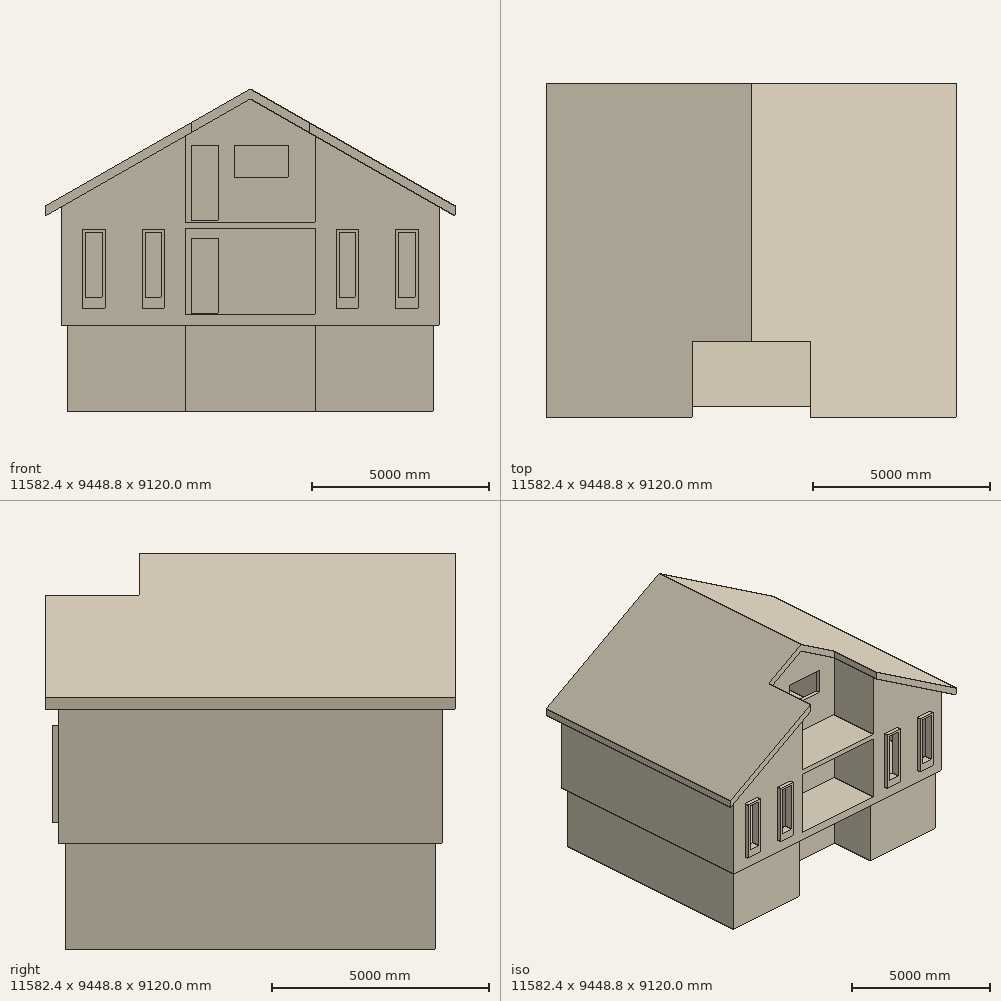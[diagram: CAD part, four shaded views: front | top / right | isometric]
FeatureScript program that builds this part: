
annotation { "Feature Type Name" : "Feature", "Feature Type Description" : "" }
export const myFeature = defineFeature(function(context is Context, id is Id, definition is map)
    precondition{}
    {
        {
            var Q0;
            Q0=qCreatedBy(makeId("Top.planeOp"),FACE);
            var sketch = newSketch(context, id + "F0", { "sketchPlane" : qUnion([Q0])});
            skLineSegment(sketch, "E0", {"start": v(0, 0) * mm, "end": v(3352.8, 0) * mm});
            skLineSegment(sketch, "E1", {"start": v(3352.8, 0) * mm, "end": v(3352.8, 1828.8) * mm});
            skLineSegment(sketch, "E2", {"start": v(3352.8, 1828.8) * mm, "end": v(7010.4, 1828.8) * mm});
            skLineSegment(sketch, "E3", {"start": v(7010.4, 1828.8) * mm, "end": v(7010.4, 0) * mm});
            skLineSegment(sketch, "E4", {"start": v(7010.4, 0) * mm, "end": v(10363.2, 0) * mm});
            skLineSegment(sketch, "E5", {"start": v(10363.2, 0) * mm, "end": v(10363.2, 8534.4) * mm});
            skLineSegment(sketch, "E6", {"start": v(10363.2, 8534.4) * mm, "end": v(7010.4, 8534.4) * mm});
            skLineSegment(sketch, "E7", {"start": v(7010.4, 8534.4) * mm, "end": v(7010.4, 7924.8) * mm});
            skLineSegment(sketch, "E8", {"start": v(7010.4, 7924.8) * mm, "end": v(3352.8, 7924.8) * mm});
            skLineSegment(sketch, "E9", {"start": v(3352.8, 7924.8) * mm, "end": v(3352.8, 8534.4) * mm});
            skLineSegment(sketch, "E10", {"start": v(3352.8, 8534.4) * mm, "end": v(0, 8534.4) * mm});
            skLineSegment(sketch, "E11", {"start": v(0, 8534.4) * mm, "end": v(0, 0) * mm});
            skSolve(sketch);
        }
        {
            var Q0;
            Q0 = qSketchRegion(id + "F0", true);
            extrude(context, id + "F1", {"entities" : qUnion([Q0]), "depth" : 2438.4 * mm});
        }
        {
            var Q0;
            Q0=makeQuery(id+"F1.opExtrude","CAP_FACE",FACE,{"disambiguationData":[OSD([sQuery(id+"F0.wireOp",EDGE,"E0"),sQuery(id+"F0.wireOp",EDGE,"E1"),sQuery(id+"F0.wireOp",EDGE,"E2"),sQuery(id+"F0.wireOp",EDGE,"E3"),sQuery(id+"F0.wireOp",EDGE,"E4"),sQuery(id+"F0.wireOp",EDGE,"E5"),sQuery(id+"F0.wireOp",EDGE,"E6"),sQuery(id+"F0.wireOp",EDGE,"E7"),sQuery(id+"F0.wireOp",EDGE,"E8"),sQuery(id+"F0.wireOp",EDGE,"E9"),sQuery(id+"F0.wireOp",EDGE,"E10"),sQuery(id+"F0.wireOp",EDGE,"E11")])],"isStart":false});
            var sketch = newSketch(context, id + "F2", { "sketchPlane" : qUnion([Q0])});
            skLineSegment(sketch, "E12.bottom", {"start": v(-152.4, -152.4) * mm, "end": v(10515.6, -152.4) * mm});
            skLineSegment(sketch, "E12.top", {"start": v(-152.4, 8686.8) * mm, "end": v(10515.6, 8686.8) * mm});
            skLineSegment(sketch, "E12.left", {"start": v(-152.4, -152.4) * mm, "end": v(-152.4, 8686.8) * mm});
            skLineSegment(sketch, "E12.right", {"start": v(10515.6, -152.4) * mm, "end": v(10515.6, 8686.8) * mm});
            skSolve(sketch);
        }
        {
            var Q0;
            Q0 = qSketchRegion(id + "F2", true);
            extrude(context, id + "F3", {"entities" : qUnion([Q0]), "operationType" : NewBodyOperationType.ADD, "depth" : 304.8 * mm});
        }
        {
            var Q0;
            Q0=makeQuery(id+"F3.opExtrude","CAP_FACE",FACE,{"disambiguationData":[OSD([sQuery(id+"F2.wireOp",EDGE,"E12.bottom"),sQuery(id+"F2.wireOp",EDGE,"E12.top"),sQuery(id+"F2.wireOp",EDGE,"E12.left"),sQuery(id+"F2.wireOp",EDGE,"E12.right")])],"isStart":false});
            var sketch = newSketch(context, id + "F4", { "sketchPlane" : qUnion([Q0])});
            skLineSegment(sketch, "E13", {"start": v(-152.4, -152.4) * mm, "end": v(3352.8, -152.4) * mm});
            skLineSegment(sketch, "E14", {"start": v(3352.8, -152.4) * mm, "end": v(3352.8, 1859.28) * mm});
            skLineSegment(sketch, "E15", {"start": v(3352.8, 1859.28) * mm, "end": v(7010.4, 1859.28) * mm});
            skLineSegment(sketch, "E16", {"start": v(7010.4, 1859.28) * mm, "end": v(7010.4, -152.4) * mm});
            skLineSegment(sketch, "E17", {"start": v(7010.4, -152.4) * mm, "end": v(10515.6, -152.4) * mm});
            skLineSegment(sketch, "E18", {"start": v(10515.6, -152.4) * mm, "end": v(10515.6, 8686.8) * mm});
            skLineSegment(sketch, "E19", {"start": v(10515.6, 8686.8) * mm, "end": v(-152.4, 8686.8) * mm});
            skLineSegment(sketch, "E20", {"start": v(-152.4, 8686.8) * mm, "end": v(-152.4, -152.4) * mm});
            skLineSegment(sketch, "E21.0", {"start": v(10363.2, 8534.4) * mm, "end": v(0, 8534.4) * mm});
            skLineSegment(sketch, "E21.1", {"start": v(10363.2, 0) * mm, "end": v(10363.2, 8534.4) * mm});
            skLineSegment(sketch, "E21.2", {"start": v(0, 8534.4) * mm, "end": v(0, 0) * mm});
            skLineSegment(sketch, "E21.3", {"start": v(7162.8, 0) * mm, "end": v(10363.2, 0) * mm});
            skLineSegment(sketch, "E21.4", {"start": v(0, 0) * mm, "end": v(3200.4, 0) * mm});
            skLineSegment(sketch, "E21.5", {"start": v(3200.4, 0) * mm, "end": v(3200.4, 2011.68) * mm});
            skLineSegment(sketch, "E21.6", {"start": v(3200.4, 2011.68) * mm, "end": v(7162.8, 2011.68) * mm});
            skLineSegment(sketch, "E21.7", {"start": v(7162.8, 2011.68) * mm, "end": v(7162.8, 0) * mm});
            skLineSegment(sketch, "E22.0", {"start": v(-147.4, 8681.8) * mm, "end": v(-147.4, -147.4) * mm});
            skLineSegment(sketch, "E22.1", {"start": v(10510.6, 8681.8) * mm, "end": v(-147.4, 8681.8) * mm});
            skLineSegment(sketch, "E22.2", {"start": v(10510.6, -147.4) * mm, "end": v(10510.6, 8681.8) * mm});
            skLineSegment(sketch, "E22.3", {"start": v(-147.4, -147.4) * mm, "end": v(3352.8, -147.4) * mm});
            skLineSegment(sketch, "E23.trimOffspring", {"start": v(7010.4, -147.4) * mm, "end": v(10510.6, -147.4) * mm});
            skSolve(sketch);
        }
        {
            var Q0;
            Q0 = qSketchRegion(id + "F4", true);
            extrude(context, id + "F5", {"entities" : qUnion([Q0]), "operationType" : NewBodyOperationType.ADD, "depth" : 6096 * mm});
        }
        {
            var Q0;
            Q0=makeQuery(id+"F5.boolean.opBoolean","MERGE",FACE,{"derivedFrom":[makeQuery(id+"F3.opExtrude","SWEPT_FACE",FACE,{"disambiguationData":[OSD([sQuery(id+"F2.wireOp",EDGE,"E12.bottom")])]}),makeQuery(id+"F5.opExtrude","SWEPT_FACE",FACE,{"disambiguationData":[OSD([sQuery(id+"F4.wireOp",EDGE,"E13")])]}),makeQuery(id+"F5.opExtrude","SWEPT_FACE",FACE,{"disambiguationData":[OSD([sQuery(id+"F4.wireOp",EDGE,"E17")])]})]});
            var sketch = newSketch(context, id + "F6", { "sketchPlane" : qUnion([Q0])});
            skLineSegment(sketch, "E24", {"start": v(5181.6, 2438.4) * mm, "end": v(5181.6, 8839.2) * mm, "construction": true});
            skLineSegment(sketch, "E25", {"start": v(5181.6, 8839.2) * mm, "end": v(-152.4, 5791.2) * mm});
            skLineSegment(sketch, "E26", {"start": v(-152.4, 5791.2) * mm, "end": v(-152.4, 14935.2) * mm});
            skLineSegment(sketch, "E27", {"start": v(-152.4, 14935.2) * mm, "end": v(10515.6, 14935.2) * mm});
            skLineSegment(sketch, "E28", {"start": v(10515.6, 14935.2) * mm, "end": v(10515.6, 5791.2) * mm});
            skLineSegment(sketch, "E29", {"start": v(10515.6, 5791.2) * mm, "end": v(5181.6, 8839.2) * mm});
            skSolve(sketch);
        }
        {
            var Q0;
            Q0 = qSketchRegion(id + "F6", true);
            extrude(context, id + "F7", {"entities" : qUnion([Q0]), "operationType" : NewBodyOperationType.REMOVE, "endBound" : BoundingType.THROUGH_ALL, "oppositeDirection" : true, "depth" : 30.48 * mm});
        }
        {
            var Q0;
            Q0=makeQuery(id+"F5.boolean.opBoolean","MERGE",FACE,{"derivedFrom":[makeQuery(id+"F3.opExtrude","SWEPT_FACE",FACE,{"disambiguationData":[OSD([sQuery(id+"F2.wireOp",EDGE,"E12.bottom")])]}),makeQuery(id+"F5.opExtrude","SWEPT_FACE",FACE,{"disambiguationData":[OSD([sQuery(id+"F4.wireOp",EDGE,"E13")])]}),makeQuery(id+"F5.opExtrude","SWEPT_FACE",FACE,{"disambiguationData":[OSD([sQuery(id+"F4.wireOp",EDGE,"E17")])]})]});
            var sketch = newSketch(context, id + "F8", { "sketchPlane" : qUnion([Q0])});
            skLineSegment(sketch, "E30.0", {"start": v(3352.8, 7794.17) * mm, "end": v(5181.6, 8839.2) * mm});
            skLineSegment(sketch, "E31.0", {"start": v(5181.6, 8839.2) * mm, "end": v(7010.4, 7794.17) * mm});
            skLineSegment(sketch, "E32.0", {"start": v(3352.8, 7794.17) * mm, "end": v(-152.4, 5791.2) * mm});
            skLineSegment(sketch, "E32.1", {"start": v(10515.6, 5791.2) * mm, "end": v(7010.4, 7794.17) * mm});
            skLineSegment(sketch, "E33", {"start": v(5181.6, 2743.2) * mm, "end": v(5181.6, 9120.04) * mm, "construction": true});
            skLineSegment(sketch, "E34", {"start": v(5181.6, 9120.04) * mm, "end": v(-609.6, 5810.79) * mm});
            skLineSegment(sketch, "E35", {"start": v(-609.6, 5810.79) * mm, "end": v(-609.6, 5529.94) * mm});
            skLineSegment(sketch, "E36", {"start": v(-609.6, 5529.94) * mm, "end": v(-152.4, 5791.2) * mm});
            skLineSegment(sketch, "E37.MirrorCS", {"start": v(5181.6, 9120.04) * mm, "end": v(10972.8, 5810.79) * mm});
            skLineSegment(sketch, "E38.MirrorCS", {"start": v(10972.8, 5810.79) * mm, "end": v(10972.8, 5529.94) * mm});
            skLineSegment(sketch, "E39.MirrorCS", {"start": v(10972.8, 5529.94) * mm, "end": v(10515.6, 5791.2) * mm});
            skSolve(sketch);
        }
        {
            var Q0;
            Q0 = qSketchRegion(id + "F8", true);
            extrude(context, id + "F9", {"entities" : qUnion([Q0]), "operationType" : NewBodyOperationType.ADD, "oppositeDirection" : true, "depth" : 9144 * mm, "hasSecondDirection" : true, "secondDirectionOppositeDirection" : false, "secondDirectionDepth" : 304.8 * mm});
        }
        {
            var Q0;
            {var subQ0=sQuery(id+"F2.wireOp",EDGE,"E12.bottom");Q0=makeQuery(id+"F5.boolean.opBoolean","SPLIT",FACE,{"disambiguationData":[TD([makeQuery(id+"F3.opExtrude","SWEPT_FACE",FACE,{"disambiguationData":[OSD([subQ0])]})])],"derivedFrom":makeQuery(id+"F3.opExtrude","CAP_FACE",FACE,{"disambiguationData":[OSD([subQ0,sQuery(id+"F2.wireOp",EDGE,"E12.top"),sQuery(id+"F2.wireOp",EDGE,"E12.left"),sQuery(id+"F2.wireOp",EDGE,"E12.right")])],"isStart":false})});}
            var sketch = newSketch(context, id + "F10", { "sketchPlane" : qUnion([Q0])});
            skLineSegment(sketch, "E40.bottom", {"start": v(3352.8, -152.4) * mm, "end": v(7010.4, -152.4) * mm});
            skLineSegment(sketch, "E40.top", {"start": v(3352.8, 1859.28) * mm, "end": v(7010.4, 1859.28) * mm});
            skLineSegment(sketch, "E40.left", {"start": v(3352.8, -152.4) * mm, "end": v(3352.8, 1859.28) * mm});
            skLineSegment(sketch, "E40.right", {"start": v(7010.4, -152.4) * mm, "end": v(7010.4, 1859.28) * mm});
            skSolve(sketch);
        }
        {
            var Q0;
            Q0 = qSketchRegion(id + "F10", true);
            extrude(context, id + "F11", {"entities" : qUnion([Q0]), "operationType" : NewBodyOperationType.ADD, "depth" : 2621.28 * mm, "hasSecondDirection" : true, "secondDirectionOppositeDirection" : false, "secondDirectionDepth" : 2438.4 * mm});
        }
        {
            var Q0;
            Q0=makeQuery(id+"F11.opExtrude","CAP_FACE",FACE,{"disambiguationData":[OSD([sQuery(id+"F10.wireOp",EDGE,"E40.bottom"),sQuery(id+"F10.wireOp",EDGE,"E40.top"),sQuery(id+"F10.wireOp",EDGE,"E40.left"),sQuery(id+"F10.wireOp",EDGE,"E40.right")])],"isStart":false});
            var sketch = newSketch(context, id + "F12", { "sketchPlane" : qUnion([Q0])});
            skLineSegment(sketch, "E41.top", {"start": v(3505.2, 1706.88) * mm, "end": v(6858, 1706.88) * mm});
            skLineSegment(sketch, "E41.left", {"start": v(3505.2, -762) * mm, "end": v(3505.2, 1706.88) * mm});
            skLineSegment(sketch, "E41.right", {"start": v(6858, -762) * mm, "end": v(6858, 1706.88) * mm});
            skLineSegment(sketch, "E42", {"start": v(3505.2, -762) * mm, "end": v(6858, -762) * mm});
            skSolve(sketch);
        }
        {
            var Q0;
            Q0 = qSketchRegion(id + "F12", true);
            extrude(context, id + "F13", {"entities" : qUnion([Q0]), "operationType" : NewBodyOperationType.REMOVE, "endBound" : BoundingType.THROUGH_ALL, "depth" : 30.48 * mm});
        }
        {
            var Q0;
            Q0=makeQuery(id+"F11.boolean.opBoolean","MERGE",FACE,{"derivedFrom":[makeQuery(id+"F5.boolean.opBoolean","MERGE",FACE,{"derivedFrom":[makeQuery(id+"F3.opExtrude","SWEPT_FACE",FACE,{"disambiguationData":[OSD([sQuery(id+"F2.wireOp",EDGE,"E12.bottom")])]}),makeQuery(id+"F5.opExtrude","SWEPT_FACE",FACE,{"disambiguationData":[OSD([sQuery(id+"F4.wireOp",EDGE,"E13")])]}),makeQuery(id+"F5.opExtrude","SWEPT_FACE",FACE,{"disambiguationData":[OSD([sQuery(id+"F4.wireOp",EDGE,"E17")])]})]}),makeQuery(id+"F11.opExtrude","SWEPT_FACE",FACE,{"disambiguationData":[OSD([sQuery(id+"F10.wireOp",EDGE,"E40.bottom")])]})]});
            var sketch = newSketch(context, id + "F14", { "sketchPlane" : qUnion([Q0])});
            skLineSegment(sketch, "E43.0", {"start": v(5181.6, 9120.04) * mm, "end": v(6858, 8162.1) * mm, "construction": true});
            skLineSegment(sketch, "E43.1", {"start": v(5181.6, 9120.04) * mm, "end": v(3505.2, 8162.1) * mm, "construction": true});
            skLineSegment(sketch, "E44", {"start": v(5181.6, 9120.04) * mm, "end": v(5181.6, 2224.24) * mm, "construction": true});
            skLineSegment(sketch, "E45.bottom", {"start": v(533.4, 3230.88) * mm, "end": v(990.6, 3230.88) * mm});
            skLineSegment(sketch, "E45.top", {"start": v(533.4, 5059.68) * mm, "end": v(990.6, 5059.68) * mm});
            skLineSegment(sketch, "E45.left", {"start": v(533.4, 3230.88) * mm, "end": v(533.4, 5059.68) * mm});
            skLineSegment(sketch, "E45.right", {"start": v(990.6, 3230.88) * mm, "end": v(990.6, 5059.68) * mm});
            skLineSegment(sketch, "E46", {"start": v(3352.8, 2743.2) * mm, "end": v(-152.4, 2743.2) * mm, "construction": true});
            skLineSegment(sketch, "E47", {"start": v(1600.2, 2743.2) * mm, "end": v(1600.2, 4776.23) * mm, "construction": true});
            skLineSegment(sketch, "E48.MirrorCS", {"start": v(2667, 3230.88) * mm, "end": v(2667, 5059.68) * mm});
            skLineSegment(sketch, "E49.MirrorCS", {"start": v(2667, 5059.68) * mm, "end": v(2209.8, 5059.68) * mm});
            skLineSegment(sketch, "E50.MirrorCS", {"start": v(2209.8, 3230.88) * mm, "end": v(2209.8, 5059.68) * mm});
            skLineSegment(sketch, "E51.MirrorCS", {"start": v(2667, 3230.88) * mm, "end": v(2209.8, 3230.88) * mm});
            skLineSegment(sketch, "E52.MirrorCS", {"start": v(7696.2, 3230.88) * mm, "end": v(8153.4, 3230.88) * mm});
            skLineSegment(sketch, "E53.MirrorCS", {"start": v(9829.8, 3230.88) * mm, "end": v(9829.8, 5059.68) * mm});
            skLineSegment(sketch, "E54.MirrorCS", {"start": v(8153.4, 3230.88) * mm, "end": v(8153.4, 5059.68) * mm});
            skLineSegment(sketch, "E55.MirrorCS", {"start": v(9829.8, 3230.88) * mm, "end": v(9372.6, 3230.88) * mm});
            skLineSegment(sketch, "E56.MirrorCS", {"start": v(9829.8, 5059.68) * mm, "end": v(9372.6, 5059.68) * mm});
            skLineSegment(sketch, "E57.MirrorCS", {"start": v(7696.2, 3230.88) * mm, "end": v(7696.2, 5059.68) * mm});
            skLineSegment(sketch, "E58.MirrorCS", {"start": v(7696.2, 5059.68) * mm, "end": v(8153.4, 5059.68) * mm});
            skLineSegment(sketch, "E59.MirrorCS", {"start": v(9372.6, 3230.88) * mm, "end": v(9372.6, 5059.68) * mm});
            skSolve(sketch);
        }
        {
            var Q0;
            Q0 = qSketchRegion(id + "F14", true);
            extrude(context, id + "F15", {"entities" : qUnion([Q0]), "operationType" : NewBodyOperationType.REMOVE, "oppositeDirection" : true, "depth" : 609.6 * mm});
        }
        {
            var Q0;
            Q0=makeQuery(id+"F11.boolean.opBoolean","SPLIT",FACE,{"disambiguationData":[TD([makeQuery(id+"F3.opExtrude","CAP_FACE",FACE,{"disambiguationData":[OSD([sQuery(id+"F2.wireOp",EDGE,"E12.bottom"),sQuery(id+"F2.wireOp",EDGE,"E12.top"),sQuery(id+"F2.wireOp",EDGE,"E12.left"),sQuery(id+"F2.wireOp",EDGE,"E12.right")])],"isStart":false})])],"derivedFrom":makeQuery(id+"F5.opExtrude","SWEPT_FACE",FACE,{"disambiguationData":[OSD([sQuery(id+"F4.wireOp",EDGE,"E15")])]})});
            var sketch = newSketch(context, id + "F16", { "sketchPlane" : qUnion([Q0])});
            skLineSegment(sketch, "E60.bottom", {"start": v(3505.2, 2773.68) * mm, "end": v(4267.2, 2773.68) * mm});
            skLineSegment(sketch, "E60.top", {"start": v(3505.2, 4907.28) * mm, "end": v(4267.2, 4907.28) * mm});
            skLineSegment(sketch, "E60.left", {"start": v(3505.2, 2773.68) * mm, "end": v(3505.2, 4907.28) * mm});
            skLineSegment(sketch, "E60.right", {"start": v(4267.2, 2773.68) * mm, "end": v(4267.2, 4907.28) * mm});
            skSolve(sketch);
        }
        {
            var Q0;
            Q0 = qSketchRegion(id + "F16", true);
            extrude(context, id + "F17", {"entities" : qUnion([Q0]), "operationType" : NewBodyOperationType.REMOVE, "oppositeDirection" : true, "depth" : 609.6 * mm});
        }
        {
            var Q0;
            Q0=makeQuery(id+"F11.boolean.opBoolean","SPLIT",FACE,{"disambiguationData":[TD([makeQuery(id+"F9.opExtrude","SWEPT_FACE",FACE,{"disambiguationData":[OSD([sQuery(id+"F8.wireOp",EDGE,"E30.0"),sQuery(id+"F8.wireOp",EDGE,"E32.0"),sQuery(id+"F8.wireOp",EDGE,"E36")])]})])],"derivedFrom":makeQuery(id+"F5.opExtrude","SWEPT_FACE",FACE,{"disambiguationData":[OSD([sQuery(id+"F4.wireOp",EDGE,"E15")])]})});
            var sketch = newSketch(context, id + "F18", { "sketchPlane" : qUnion([Q0])});
            skLineSegment(sketch, "E61.bottom", {"start": v(3505.2, 5394.96) * mm, "end": v(4267.2, 5394.96) * mm});
            skLineSegment(sketch, "E61.top", {"start": v(3505.2, 7528.56) * mm, "end": v(4267.2, 7528.56) * mm});
            skLineSegment(sketch, "E61.left", {"start": v(3505.2, 5394.96) * mm, "end": v(3505.2, 7528.56) * mm});
            skLineSegment(sketch, "E61.right", {"start": v(4267.2, 5394.96) * mm, "end": v(4267.2, 7528.56) * mm});
            skLineSegment(sketch, "E62.bottom", {"start": v(4724.4, 7528.56) * mm, "end": v(6248.4, 7528.56) * mm});
            skLineSegment(sketch, "E62.top", {"start": v(4724.4, 6614.16) * mm, "end": v(6248.4, 6614.16) * mm});
            skLineSegment(sketch, "E62.left", {"start": v(4724.4, 7528.56) * mm, "end": v(4724.4, 6614.16) * mm});
            skLineSegment(sketch, "E62.right", {"start": v(6248.4, 7528.56) * mm, "end": v(6248.4, 6614.16) * mm});
            skSolve(sketch);
        }
        {
            var Q0;
            Q0 = qSketchRegion(id + "F18", true);
            extrude(context, id + "F19", {"entities" : qUnion([Q0]), "operationType" : NewBodyOperationType.REMOVE, "oppositeDirection" : true, "depth" : 609.6 * mm});
        }
        {
            var Q0;
            Q0=makeQuery(id+"F11.boolean.opBoolean","MERGE",FACE,{"derivedFrom":[makeQuery(id+"F5.boolean.opBoolean","MERGE",FACE,{"derivedFrom":[makeQuery(id+"F3.opExtrude","SWEPT_FACE",FACE,{"disambiguationData":[OSD([sQuery(id+"F2.wireOp",EDGE,"E12.bottom")])]}),makeQuery(id+"F5.opExtrude","SWEPT_FACE",FACE,{"disambiguationData":[OSD([sQuery(id+"F4.wireOp",EDGE,"E13")])]}),makeQuery(id+"F5.opExtrude","SWEPT_FACE",FACE,{"disambiguationData":[OSD([sQuery(id+"F4.wireOp",EDGE,"E17")])]})]}),makeQuery(id+"F11.opExtrude","SWEPT_FACE",FACE,{"disambiguationData":[OSD([sQuery(id+"F10.wireOp",EDGE,"E40.bottom")])]})]});
            var sketch = newSketch(context, id + "F20", { "sketchPlane" : qUnion([Q0])});
            skLineSegment(sketch, "E63.0", {"start": v(533.4, 3230.88) * mm, "end": v(533.4, 5059.68) * mm});
            skLineSegment(sketch, "E63.1", {"start": v(533.4, 5059.68) * mm, "end": v(990.6, 5059.68) * mm});
            skLineSegment(sketch, "E63.2", {"start": v(990.6, 3230.88) * mm, "end": v(990.6, 5059.68) * mm});
            skLineSegment(sketch, "E63.3", {"start": v(533.4, 3230.88) * mm, "end": v(990.6, 3230.88) * mm});
            skLineSegment(sketch, "E64.bottom", {"start": v(441.96, 5151.12) * mm, "end": v(1082.04, 5151.12) * mm});
            skLineSegment(sketch, "E64.top", {"start": v(441.96, 2926.08) * mm, "end": v(1082.04, 2926.08) * mm});
            skLineSegment(sketch, "E64.left", {"start": v(441.96, 5151.12) * mm, "end": v(441.96, 2926.08) * mm});
            skLineSegment(sketch, "E64.right", {"start": v(1082.04, 5151.12) * mm, "end": v(1082.04, 2926.08) * mm});
            skLineSegment(sketch, "E65", {"start": v(3352.8, 2743.2) * mm, "end": v(-152.4, 2743.2) * mm, "construction": true});
            skLineSegment(sketch, "E66", {"start": v(1600.2, 2743.2) * mm, "end": v(1600.2, 4787.63) * mm, "construction": true});
            skPoint(sketch, "E66.endSnap0", {"position": v(1600.2, 2743.2) * mm});
            skLineSegment(sketch, "E67", {"start": v(5181.6, 2438.4) * mm, "end": v(5181.6, 3121.5) * mm, "construction": true});
            skLineSegment(sketch, "E68.MirrorCS", {"start": v(2667, 5059.68) * mm, "end": v(2209.8, 5059.68) * mm});
            skLineSegment(sketch, "E69.MirrorCS", {"start": v(2667, 3230.88) * mm, "end": v(2667, 5059.68) * mm});
            skLineSegment(sketch, "E70.MirrorCS", {"start": v(2209.8, 3230.88) * mm, "end": v(2209.8, 5059.68) * mm});
            skLineSegment(sketch, "E71.MirrorCS", {"start": v(2667, 3230.88) * mm, "end": v(2209.8, 3230.88) * mm});
            skLineSegment(sketch, "E72.MirrorCS", {"start": v(2758.44, 5151.12) * mm, "end": v(2118.36, 5151.12) * mm});
            skLineSegment(sketch, "E73.MirrorCS", {"start": v(2758.44, 2926.08) * mm, "end": v(2118.36, 2926.08) * mm});
            skLineSegment(sketch, "E74.MirrorCS", {"start": v(2118.36, 5151.12) * mm, "end": v(2118.36, 2926.08) * mm});
            skLineSegment(sketch, "E75.MirrorCS", {"start": v(2758.44, 5151.12) * mm, "end": v(2758.44, 2926.08) * mm});
            skLineSegment(sketch, "E76.MirrorCS", {"start": v(9829.8, 5059.68) * mm, "end": v(9372.6, 5059.68) * mm});
            skLineSegment(sketch, "E77.MirrorCS", {"start": v(9829.8, 3230.88) * mm, "end": v(9829.8, 5059.68) * mm});
            skLineSegment(sketch, "E78.MirrorCS", {"start": v(7604.76, 5151.12) * mm, "end": v(8244.84, 5151.12) * mm});
            skLineSegment(sketch, "E79.MirrorCS", {"start": v(7696.2, 3230.88) * mm, "end": v(8153.4, 3230.88) * mm});
            skLineSegment(sketch, "E80.MirrorCS", {"start": v(7604.76, 2926.08) * mm, "end": v(8244.84, 2926.08) * mm});
            skLineSegment(sketch, "E81.MirrorCS", {"start": v(8153.4, 3230.88) * mm, "end": v(8153.4, 5059.68) * mm});
            skLineSegment(sketch, "E82.MirrorCS", {"start": v(7604.76, 5151.12) * mm, "end": v(7604.76, 2926.08) * mm});
            skPoint(sketch, "E83.MirrorP", {"position": v(8763, 2743.2) * mm});
            skLineSegment(sketch, "E84.MirrorCS", {"start": v(8244.84, 5151.12) * mm, "end": v(8244.84, 2926.08) * mm});
            skLineSegment(sketch, "E85.MirrorCS", {"start": v(9372.6, 3230.88) * mm, "end": v(9372.6, 5059.68) * mm});
            skLineSegment(sketch, "E86.MirrorCS", {"start": v(9829.8, 3230.88) * mm, "end": v(9372.6, 3230.88) * mm});
            skLineSegment(sketch, "E87.MirrorCS", {"start": v(9921.24, 5151.12) * mm, "end": v(9281.16, 5151.12) * mm});
            skLineSegment(sketch, "E88.MirrorCS", {"start": v(9921.24, 2926.08) * mm, "end": v(9281.16, 2926.08) * mm});
            skLineSegment(sketch, "E89.MirrorCS", {"start": v(9921.24, 5151.12) * mm, "end": v(9921.24, 2926.08) * mm});
            skLineSegment(sketch, "E90.MirrorCS", {"start": v(9281.16, 5151.12) * mm, "end": v(9281.16, 2926.08) * mm});
            skLineSegment(sketch, "E91.MirrorCS", {"start": v(7696.2, 5059.68) * mm, "end": v(8153.4, 5059.68) * mm});
            skLineSegment(sketch, "E92.MirrorCS", {"start": v(7696.2, 3230.88) * mm, "end": v(7696.2, 5059.68) * mm});
            skSolve(sketch);
        }
        {
            var Q0;
            Q0 = qSketchRegion(id + "F20", true);
            extrude(context, id + "F21", {"entities" : qUnion([Q0]), "operationType" : NewBodyOperationType.ADD, "depth" : 152.4 * mm});
        }
    });
